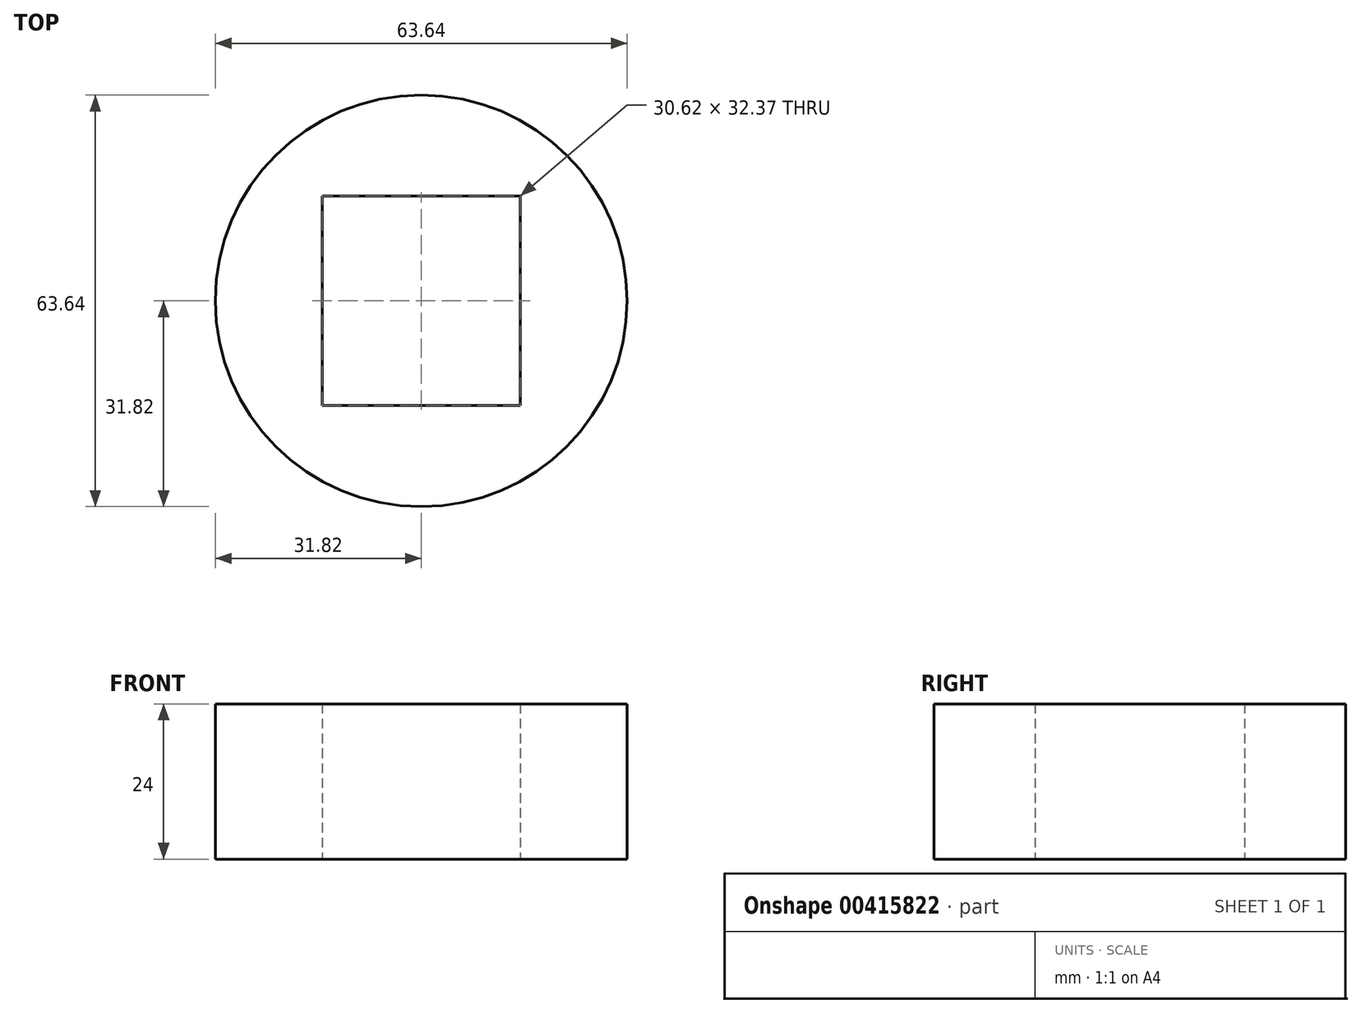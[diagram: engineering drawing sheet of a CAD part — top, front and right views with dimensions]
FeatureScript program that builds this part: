
annotation { "Feature Type Name" : "Feature", "Feature Type Description" : "" }
export const myFeature = defineFeature(function(context is Context, id is Id, definition is map)
    precondition{}
    {
        {
            var Q0;
            Q0=qCreatedBy(makeId("Top.planeOp"),FACE);
            var sketch = newSketch(context, id + "F0", { "sketchPlane" : qUnion([Q0])});
            skCircle(sketch, "E0", {"center": v(0, 0) * mm, "radius": 22.28 * mm});
            skLineSegment(sketch, "E1.bottom", {"start": v(15.3, -16.19) * mm, "end": v(-15.3, -16.19) * mm});
            skLineSegment(sketch, "E1.top", {"start": v(15.3, 16.19) * mm, "end": v(-15.3, 16.19) * mm});
            skLineSegment(sketch, "E1.left", {"start": v(15.3, -16.19) * mm, "end": v(15.3, 16.19) * mm});
            skLineSegment(sketch, "E1.right", {"start": v(-15.3, -16.19) * mm, "end": v(-15.3, 16.19) * mm});
            skSolve(sketch);
        }
        {
            var Q0;
            Q0=makeQuery(id+"F0.imprint","IMPRINT",FACE,{"disambiguationData":[TD([[makeQuery(id+"F0.imprint","IMPRINT",EDGE,{"derivedFrom":sQuery(id+"F0.wireOp",EDGE,"E1.bottom")}),-1.0]])]});
            extrude(context, id + "F1", {"entities" : qUnion([Q0]), "depth" : 25 * mm});
        }
        {
            var Q0;
            Q0=qCreatedBy(makeId("Top.planeOp"),FACE);
            var sketch = newSketch(context, id + "F2", { "sketchPlane" : qUnion([Q0])});
            skCircle(sketch, "E2", {"center": v(0, 0) * mm, "radius": 31.82 * mm});
            skSolve(sketch);
        }
        {
            var Q0;
            Q0 = qSketchRegion(id + "F2", true);
            extrude(context, id + "F3", {"entities" : qUnion([Q0]), "depth" : 24 * mm});
        }
        {
            var Q0;
            Q0=makeQuery(id+"F1.opExtrude","SWEPT_BODY",BODY,{"disambiguationData":[OSD([sQuery(id+"F0.wireOp",EDGE,"E1.bottom"),sQuery(id+"F0.wireOp",EDGE,"E1.top"),sQuery(id+"F0.wireOp",EDGE,"E1.left"),sQuery(id+"F0.wireOp",EDGE,"E1.right")])]});
            var Q1;
            Q1=makeQuery(id+"F3.opExtrude","SWEPT_BODY",BODY,{"disambiguationData":[OSD([sQuery(id+"F2.wireOp",EDGE,"E2")])]});
            booleanBodies(context, id + "F4", {"operationType" : BooleanOperationType.SUBTRACTION, "tools" : qUnion([Q0]), "targets" : qUnion([Q1])});
        }
    });
